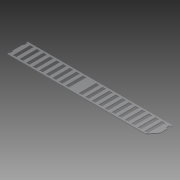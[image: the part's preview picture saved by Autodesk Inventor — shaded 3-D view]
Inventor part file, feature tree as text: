
AUTODESK INVENTOR PART (.ipt)
format: ipt  version: 2013 (Build 170138000, 138)  size: 243,712 bytes
history: native  units: in
note: dims shown in document units (in); Inventor stores cm internally (conversion verified against a paired STEP export)
features: extrude x5, sketch x5, projected_geometry x2
ambient origin geometry x8: Origin, YZ Plane, XZ Plane, XY Plane, X Axis, Y Axis, Z Axis, Center Point
bodies: Solid1 (feature_tree)
feature tree (12):
  extrude  "Extrusion1"  Depth=22.0in
  extrude  "Extrusion2"  Depth=0.5in
  extrude  "Extrusion3"  Depth=0.5in
  extrude  "Extrusion4"  Depth=0.125in TaperAngle=0.0deg
  extrude  "Extrusion5"  Depth=0.5in
  sketch  "Sketch1"  dims[d0=3.125in d1=22.0in]
  sketch  "Sketch3"  dims[d2=0.125in d3=0.0in d4=0.5in]
  sketch  "Sketch4"  dims[d5=0.25in d6=0.5in]
  projected_geometry  "Projected Loop1"
  projected_geometry  "Projected Loop2"
  sketch  "Sketch5"  dims[d7=0.25in d8=0.125in d9=0.0in]
  sketch  "Sketch6"  dims[d10=0.25in d11=0.0in d12=0.5in d14=0.625in d15=0.25in d16=0.25in d17=8.2677in d19=1.0in d20=0.3937in d22=1.0in d24=1.0in d25=0.0in d26=0.3436in d27=1.0in d28=1.0in d29=0.0in]
